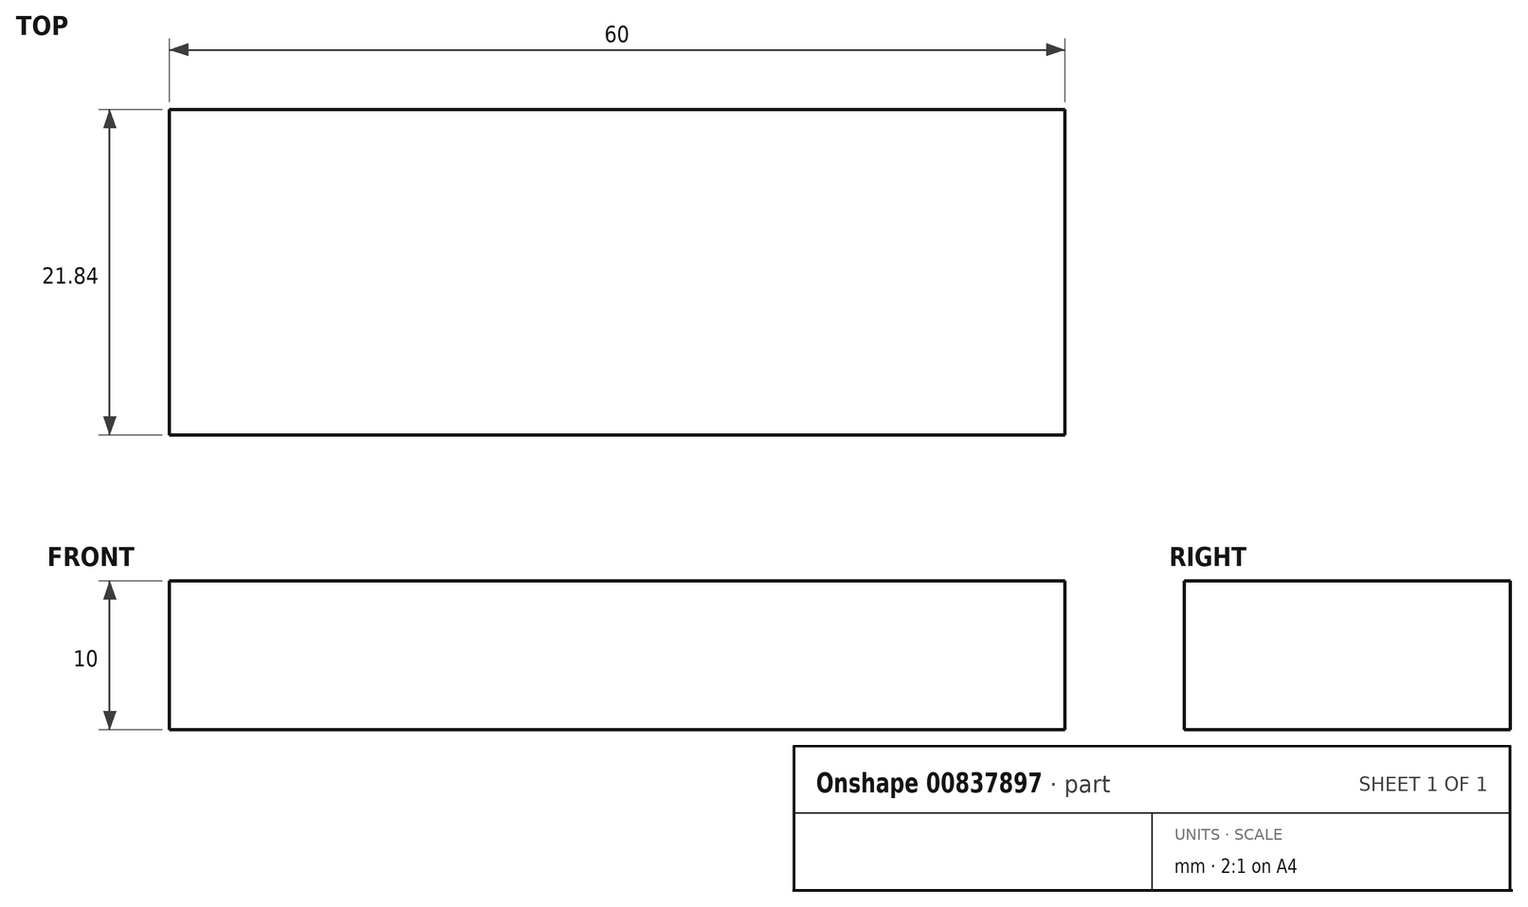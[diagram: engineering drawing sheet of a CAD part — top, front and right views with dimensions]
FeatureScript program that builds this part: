
annotation { "Feature Type Name" : "Feature", "Feature Type Description" : "" }
export const myFeature = defineFeature(function(context is Context, id is Id, definition is map)
    precondition{}
    {
        {
            var Q0;
            Q0=qCreatedBy(makeId("Top.planeOp"),FACE);
            var sketch = newSketch(context, id + "F0", { "sketchPlane" : qUnion([Q0])});
            skLineSegment(sketch, "E0.bottom", {"start": v(30, -10.92) * mm, "end": v(-30, -10.92) * mm});
            skLineSegment(sketch, "E0.top", {"start": v(30, 10.92) * mm, "end": v(-30, 10.92) * mm});
            skLineSegment(sketch, "E0.left", {"start": v(30, -10.92) * mm, "end": v(30, 10.92) * mm});
            skLineSegment(sketch, "E0.right", {"start": v(-30, -10.92) * mm, "end": v(-30, 10.92) * mm});
            skPoint(sketch, "E0.middle", {"position": v(0, 0) * mm});
            skSolve(sketch);
        }
        {
            var Q0;
            Q0=makeQuery(id+"F0.imprint","IMPRINT",FACE,{"disambiguationData":[TD([[makeQuery(id+"F0.imprint","IMPRINT",EDGE,{"derivedFrom":sQuery(id+"F0.wireOp",EDGE,"E0.bottom")}),-1.0]])]});
            extrude(context, id + "F1", {"entities" : qUnion([Q0]), "depth" : 10 * mm, "offsetDistance" : 25.4 * mm});
        }
    });
